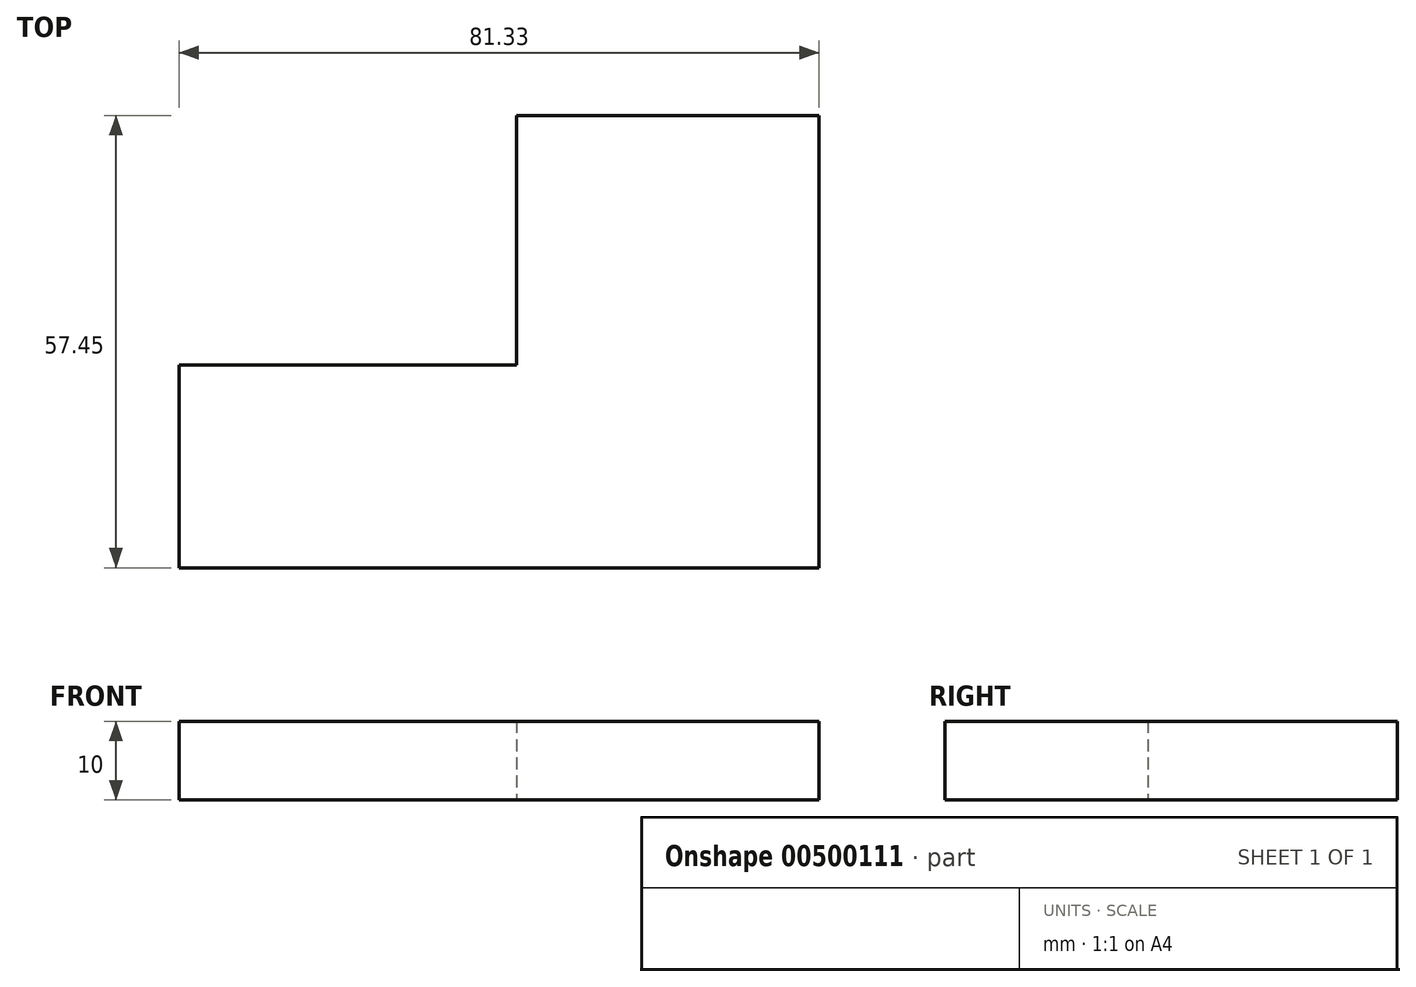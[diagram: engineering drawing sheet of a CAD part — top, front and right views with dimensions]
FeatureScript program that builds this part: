
annotation { "Feature Type Name" : "Feature", "Feature Type Description" : "" }
export const myFeature = defineFeature(function(context is Context, id is Id, definition is map)
    precondition{}
    {
        {
            var Q0;
            Q0=qCreatedBy(makeId("Top.planeOp"),FACE);
            var sketch = newSketch(context, id + "F0", { "sketchPlane" : qUnion([Q0])});
            skLineSegment(sketch, "E0", {"start": v(-48.87, 0) * mm, "end": v(-48.87, 25.74) * mm});
            skLineSegment(sketch, "E1", {"start": v(-48.87, 25.74) * mm, "end": v(-5.97, 25.74) * mm});
            skLineSegment(sketch, "E2", {"start": v(-5.97, 25.74) * mm, "end": v(-5.97, 57.45) * mm});
            skLineSegment(sketch, "E3", {"start": v(-5.97, 57.45) * mm, "end": v(32.46, 57.45) * mm});
            skLineSegment(sketch, "E4", {"start": v(32.46, 57.45) * mm, "end": v(32.46, 0) * mm});
            skLineSegment(sketch, "E5", {"start": v(32.46, 0) * mm, "end": v(-48.87, 0) * mm});
            skSolve(sketch);
        }
        {
            var Q0;
            Q0=makeQuery(id+"F0.imprint","IMPRINT",FACE,{"disambiguationData":[TD([[makeQuery(id+"F0.imprint","IMPRINT",EDGE,{"derivedFrom":sQuery(id+"F0.wireOp",EDGE,"E0")}),-1.0]])]});
            extrude(context, id + "F1", {"entities" : qUnion([Q0]), "depth" : 10 * mm});
        }
    });
